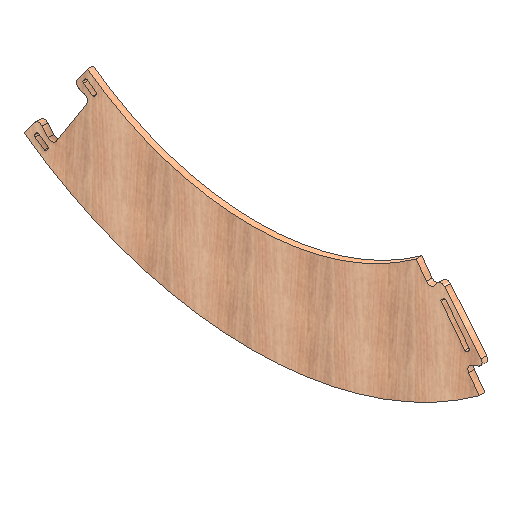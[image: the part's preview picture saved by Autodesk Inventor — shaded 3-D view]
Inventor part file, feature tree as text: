
AUTODESK INVENTOR PART (.ipt)
format: ipt  version: 2021 (Build 250183000, 183)  size: 270,336 bytes
history: native  units: mm
features: other x2, extrude x2, hole x1
ambient origin geometry x8: Origin, YZ Plane, XZ Plane, XY Plane, X Axis, Y Axis, Z Axis, Center Point
bodies: Solid1 (feature_tree)
feature tree (5):
  other  "CONTOURS"
  hole  "HOLES"  [1 undecoded]
  other  "LETTERS"
  extrude  "Extrusion1"  Depth=18.0mm TaperAngle=0.0deg
  extrude  "Extrusion2"  [1 undecoded]
note: 2 required parameter values undecoded (feature->parameter linkage not recoverable at this tier; creation-order binding heuristic only, values carry confidence <= 0.55)
